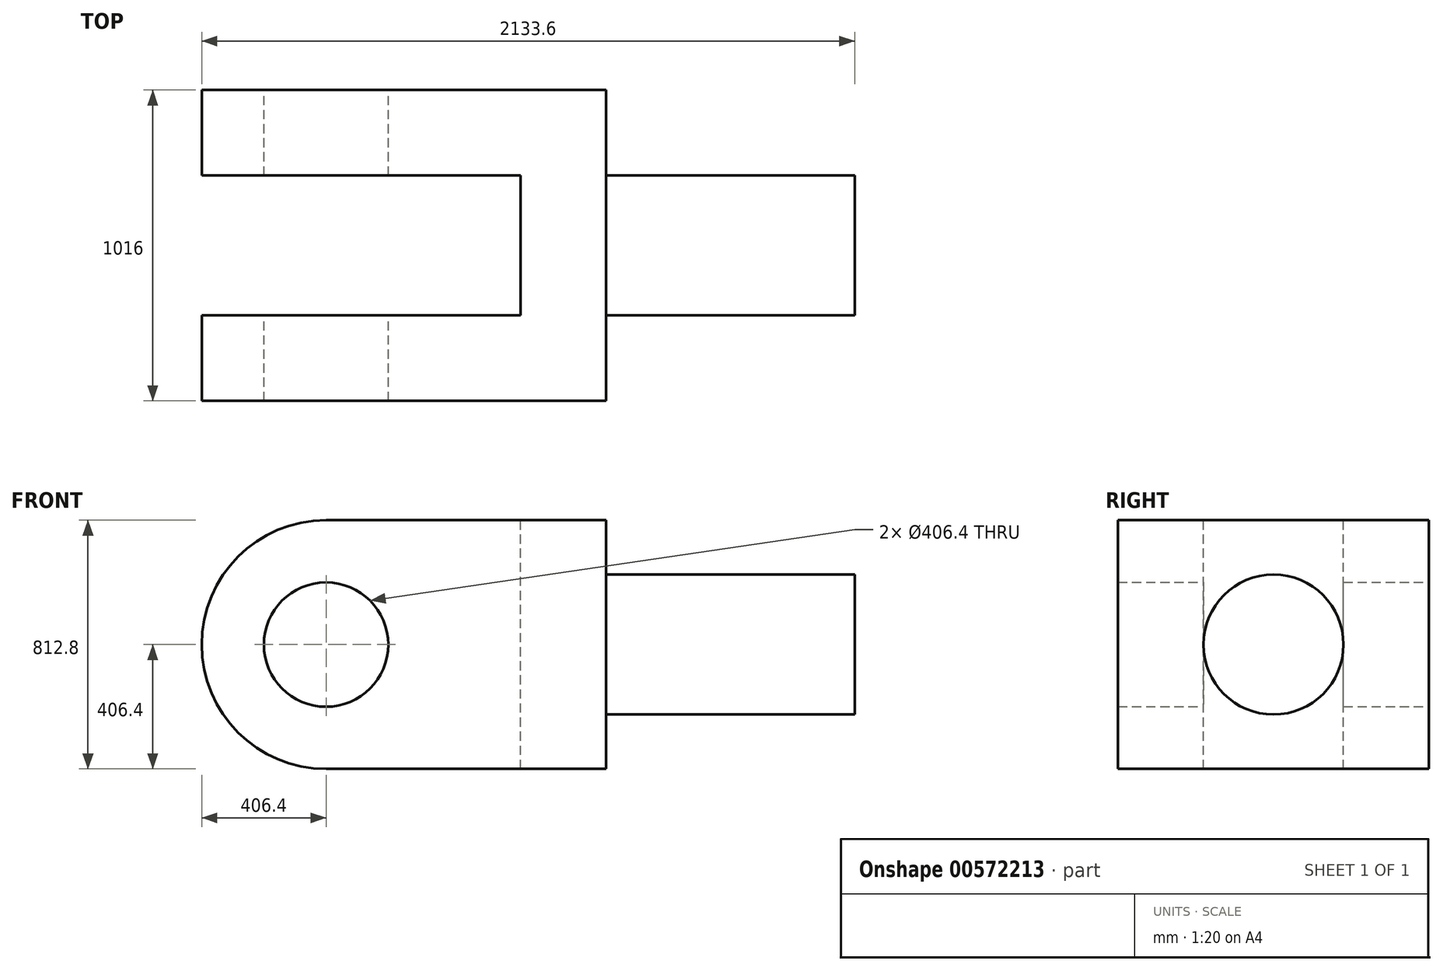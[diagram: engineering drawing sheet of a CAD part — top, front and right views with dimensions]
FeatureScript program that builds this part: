
annotation { "Feature Type Name" : "Feature", "Feature Type Description" : "" }
export const myFeature = defineFeature(function(context is Context, id is Id, definition is map)
    precondition{}
    {
        {
            var Q0;
            Q0=qCreatedBy(makeId("Front.planeOp"),FACE);
            var sketch = newSketch(context, id + "F0", { "sketchPlane" : qUnion([Q0])});
            skCircle(sketch, "E0", {"center": v(0, 0) * mm, "radius": 203.2 * mm});
            skCircle(sketch, "E1", {"center": v(0, 0) * mm, "radius": 406.4 * mm});
            skLineSegment(sketch, "E2", {"start": v(0, 406.4) * mm, "end": v(914.4, 406.4) * mm});
            skLineSegment(sketch, "E3", {"start": v(0, -406.4) * mm, "end": v(914.4, -406.4) * mm});
            skLineSegment(sketch, "E4", {"start": v(914.4, -406.4) * mm, "end": v(914.4, -228.6) * mm});
            skLineSegment(sketch, "E5", {"start": v(914.4, -228.6) * mm, "end": v(1727.2, -228.6) * mm});
            skLineSegment(sketch, "E6", {"start": v(1727.2, -228.6) * mm, "end": v(1727.2, 228.6) * mm});
            skLineSegment(sketch, "E7", {"start": v(1727.2, 228.6) * mm, "end": v(914.4, 228.6) * mm});
            skLineSegment(sketch, "E8", {"start": v(914.4, 228.6) * mm, "end": v(914.4, 406.4) * mm});
            skSolve(sketch);
        }
        {
            var Q0;
            Q0 = qSketchRegion(id + "F0", true);
            extrude(context, id + "F1", {"entities" : qUnion([Q0]), "depth" : 1016 * mm, "offsetDistance" : 25.4 * mm});
        }
        {
            var Q0;
            Q0=makeQuery(id+"F1.opExtrude","SWEPT_FACE",FACE,{"disambiguationData":[OSD([sQuery(id+"F0.wireOp",EDGE,"E2")])]});
            var sketch = newSketch(context, id + "F2", { "sketchPlane" : qUnion([Q0])});
            skLineSegment(sketch, "E9", {"start": v(0, 0) * mm, "end": v(0, -279.4) * mm});
            skLineSegment(sketch, "E10", {"start": v(0, -736.6) * mm, "end": v(0, -1016) * mm});
            skLineSegment(sketch, "E11", {"start": v(0, -736.6) * mm, "end": v(-406.4, -736.6) * mm});
            skLineSegment(sketch, "E12", {"start": v(0, -279.4) * mm, "end": v(-406.4, -279.4) * mm});
            skLineSegment(sketch, "E13", {"start": v(-406.4, -279.4) * mm, "end": v(-406.4, -736.6) * mm});
            skLineSegment(sketch, "E14", {"start": v(-406.4, -279.4) * mm, "end": v(0, -279.4) * mm});
            skLineSegment(sketch, "E15", {"start": v(-406.4, -736.6) * mm, "end": v(0, -736.6) * mm});
            skLineSegment(sketch, "E16", {"start": v(0, -736.6) * mm, "end": v(0, -279.4) * mm});
            skLineSegment(sketch, "E17", {"start": v(0, -279.4) * mm, "end": v(-279.4, -279.4) * mm});
            skLineSegment(sketch, "E18", {"start": v(-279.4, -279.4) * mm, "end": v(-279.4, -736.6) * mm});
            skLineSegment(sketch, "E19", {"start": v(-279.4, -736.6) * mm, "end": v(0, -736.6) * mm});
            skLineSegment(sketch, "E20", {"start": v(-406.4, -279.4) * mm, "end": v(635, -279.4) * mm});
            skLineSegment(sketch, "E21", {"start": v(635, -279.4) * mm, "end": v(635, -736.6) * mm});
            skLineSegment(sketch, "E22", {"start": v(635, -736.6) * mm, "end": v(0, -736.6) * mm});
            skSolve(sketch);
        }
        {
            var Q0;
            {var subQ3=sQuery(id+"F2.wireOp",EDGE,"E18");Q0=makeQuery(id+"F2.imprint","IMPRINT",FACE,{"disambiguationData":[TD([[makeQuery(id+"F2.imprint","IMPRINT",EDGE,{"derivedFrom":subQ3}),-1.0]])]});}
            var Q1;
            {var subQ0=sQuery(id+"F2.wireOp",EDGE,"E13");Q1=makeQuery(id+"F2.imprint","IMPRINT",FACE,{"disambiguationData":[TD([[makeQuery(id+"F2.imprint","IMPRINT",EDGE,{"derivedFrom":subQ0}),1.0]])]});}
            extrude(context, id + "F3", {"entities" : qUnion([Q0, Q1]), "operationType" : NewBodyOperationType.REMOVE, "endBound" : BoundingType.THROUGH_ALL, "oppositeDirection" : true, "depth" : 25.4 * mm, "offsetDistance" : 25.4 * mm});
        }
        {
            var Q0;
            {var subQ0=sQuery(id+"F2.wireOp",EDGE,"E16");Q0=makeQuery(id+"F2.imprint","IMPRINT",FACE,{"disambiguationData":[TD([[makeQuery(id+"F2.imprint","IMPRINT",EDGE,{"derivedFrom":subQ0}),-1.0]])]});}
            var Q1;
            {var subQ0=sQuery(id+"F2.wireOp",EDGE,"E16");Q1=makeQuery(id+"F2.imprint","IMPRINT",FACE,{"disambiguationData":[TD([[makeQuery(id+"F2.imprint","IMPRINT",EDGE,{"derivedFrom":subQ0}),1.0]])]});}
            var Q2;
            {var subQ0=sQuery(id+"F2.wireOp",EDGE,"E13");Q2=makeQuery(id+"F2.imprint","IMPRINT",FACE,{"disambiguationData":[TD([[makeQuery(id+"F2.imprint","IMPRINT",EDGE,{"derivedFrom":subQ0}),1.0]])]});}
            extrude(context, id + "F4", {"entities" : qUnion([Q0, Q1, Q2]), "operationType" : NewBodyOperationType.REMOVE, "endBound" : BoundingType.THROUGH_ALL, "oppositeDirection" : true, "depth" : 25.4 * mm, "offsetDistance" : 25.4 * mm});
        }
        {
            var Q0;
            Q0=makeQuery(id+"F1.opExtrude","SWEPT_FACE",FACE,{"disambiguationData":[OSD([sQuery(id+"F0.wireOp",EDGE,"E7")])]});
            var sketch = newSketch(context, id + "F5", { "sketchPlane" : qUnion([Q0])});
            skLineSegment(sketch, "E23", {"start": v(1727.2, 0) * mm, "end": v(1727.2, -279.4) * mm});
            skLineSegment(sketch, "E24", {"start": v(1727.2, -279.4) * mm, "end": v(914.4, -279.4) * mm});
            skLineSegment(sketch, "E25", {"start": v(1727.2, -1016) * mm, "end": v(1727.2, -736.6) * mm});
            skLineSegment(sketch, "E26", {"start": v(1727.2, -736.6) * mm, "end": v(914.4, -736.6) * mm});
            skSolve(sketch);
        }
        {
            var Q0;
            Q0=makeQuery(id+"F5.imprint","IMPRINT",FACE,{"disambiguationData":[TD([[makeQuery(id+"F5.imprint","IMPRINT",EDGE,{"derivedFrom":sQuery(id+"F5.wireOp",EDGE,"E23")}),1.0]])]});
            var Q1;
            Q1=makeQuery(id+"F5.imprint","IMPRINT",FACE,{"disambiguationData":[TD([[makeQuery(id+"F5.imprint","IMPRINT",EDGE,{"derivedFrom":sQuery(id+"F5.wireOp",EDGE,"E25")}),1.0]])]});
            extrude(context, id + "F6", {"entities" : qUnion([Q0, Q1]), "operationType" : NewBodyOperationType.REMOVE, "endBound" : BoundingType.THROUGH_ALL, "oppositeDirection" : true, "depth" : 25.4 * mm, "offsetDistance" : 25.4 * mm});
        }
        {
            var Q0;
            Q0=makeQuery(id+"F1.opExtrude","SWEPT_FACE",FACE,{"disambiguationData":[OSD([sQuery(id+"F0.wireOp",EDGE,"E6")])]});
            var sketch = newSketch(context, id + "F7", { "sketchPlane" : qUnion([Q0])});
            skCircle(sketch, "E27", {"center": v(-508, 0) * mm, "radius": 228.6 * mm});
            skPoint(sketch, "E27.centerSnap0", {"position": v(-508, 228.6) * mm});
            skSolve(sketch);
        }
        {
            var Q0;
            {var subQ0=sQuery(id+"F7.wireOp",EDGE,"E27");var subQ1=sQuery(id+"F0.wireOp",EDGE,"E7");var subQ2=sQuery(id+"F0.wireOp",EDGE,"E6");var subQ3=makeQuery(id+"F1.opExtrude","SWEPT_EDGE",EDGE,{"disambiguationData":[OSD([subQ2,subQ1])]});var subQ4=makeQuery(id+"F7.imprint","INTERSECT",VERTEX,{"derivedFrom":[subQ3,subQ0]});Q0=makeQuery(id+"F7.imprint","IMPRINT",FACE,{"disambiguationData":[TD([[makeQuery(id+"F7.imprint","IMPRINT",EDGE,{"disambiguationData":[TD([[subQ4,-1.0]])],"derivedFrom":subQ0}),-1.0]])]});}
            var Q1;
            {var subQ0=sQuery(id+"F7.wireOp",EDGE,"E27");var subQ1=sQuery(id+"F0.wireOp",EDGE,"E6");var subQ4=makeQuery(id+"F1.opExtrude","SWEPT_EDGE",EDGE,{"disambiguationData":[OSD([sQuery(id+"F0.wireOp",EDGE,"E5"),subQ1])]});var subQ5=makeQuery(id+"F7.imprint","INTERSECT",VERTEX,{"derivedFrom":[subQ4,subQ0]});Q1=makeQuery(id+"F7.imprint","IMPRINT",FACE,{"disambiguationData":[TD([[makeQuery(id+"F7.imprint","IMPRINT",EDGE,{"disambiguationData":[TD([[subQ5,1.0]])],"derivedFrom":subQ0}),-1.0]])]});}
            var Q2;
            {var subQ0=sQuery(id+"F7.wireOp",EDGE,"E27");var subQ1=sQuery(id+"F0.wireOp",EDGE,"E6");var subQ4=makeQuery(id+"F1.opExtrude","SWEPT_EDGE",EDGE,{"disambiguationData":[OSD([sQuery(id+"F0.wireOp",EDGE,"E5"),subQ1])]});var subQ5=makeQuery(id+"F7.imprint","INTERSECT",VERTEX,{"derivedFrom":[subQ4,subQ0]});Q2=makeQuery(id+"F7.imprint","IMPRINT",FACE,{"disambiguationData":[TD([[makeQuery(id+"F7.imprint","IMPRINT",EDGE,{"disambiguationData":[TD([[subQ5,-1.0]])],"derivedFrom":subQ0}),-1.0]])]});}
            var Q3;
            {var subQ0=sQuery(id+"F7.wireOp",EDGE,"E27");var subQ1=sQuery(id+"F0.wireOp",EDGE,"E7");var subQ2=sQuery(id+"F0.wireOp",EDGE,"E6");var subQ3=makeQuery(id+"F1.opExtrude","SWEPT_EDGE",EDGE,{"disambiguationData":[OSD([subQ2,subQ1])]});var subQ4=makeQuery(id+"F7.imprint","INTERSECT",VERTEX,{"derivedFrom":[subQ3,subQ0]});Q3=makeQuery(id+"F7.imprint","IMPRINT",FACE,{"disambiguationData":[TD([[makeQuery(id+"F7.imprint","IMPRINT",EDGE,{"disambiguationData":[TD([[subQ4,1.0]])],"derivedFrom":subQ0}),-1.0]])]});}
            extrude(context, id + "F8", {"entities" : qUnion([Q0, Q1, Q2, Q3]), "operationType" : NewBodyOperationType.REMOVE, "oppositeDirection" : true, "depth" : 812.8 * mm, "offsetDistance" : 25.4 * mm});
        }
    });
